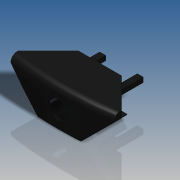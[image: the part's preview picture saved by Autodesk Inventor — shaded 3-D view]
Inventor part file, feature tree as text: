
AUTODESK INVENTOR PART (.ipt)
format: ipt  version: 2016 SP2 (Build 200236200, 236)  size: 336,896 bytes
history: native  units: in
note: dims shown in document units (in); Inventor stores cm internally (conversion verified against a paired STEP export)
features: extrude x6, sketch x5, projected_geometry x3, fillet x2, plane x1
ambient origin geometry x8: Origin, YZ Plane, XZ Plane, XY Plane, X Axis, Y Axis, Z Axis, Center Point
bodies: Solid1 (feature_tree)
feature tree (17):
  extrude  "Extrusion1"  Depth=0.7559in
  extrude  "Extrusion2"  Depth=0.3051in
  extrude  "Extrusion3"  Depth=0.1136in
  plane  "Work Plane1"
  sketch  "Sketch5"  dims[d8=0.014in d9=0.0472in]
  extrude  "Extrusion4"  Depth=0.0472in
  extrude  "Extrusion5"  Depth=0.2205in TaperAngle=0.0deg
  extrude  "Extrusion6"  Depth=0.0378in
  fillet  "Fillet2"  Radius=0.0472in
  fillet  "Fillet1"  Radius=0.0394in
  sketch  "Sketch2"  dims[d0=2.4409in d1=0.7559in]
  sketch  "Sketch3"  dims[d2=0.315in d3=0.3051in]
  sketch  "Sketch4"  dims[d5=0.2693in d6=0.0in d7=0.1136in]
  projected_geometry  "Projected Loop1"
  sketch  "Sketch6"  dims[d10=0.0472in d11=0.2205in d12=0.0in d13=0.0378in d14=0.0472in d15=0.0394in d16=0.378in d17=0.0in d18=0.0507in d19=0.315in d20=0.1276in d21=0.126in d22=0.378in d23=0.0in d24=0.2835in d25=0.0in d26=0.2835in d27=0.0in d28=0.0039in d29=0.0472in d30=0.0547in]
  projected_geometry  "Projected Loop2"
  projected_geometry  "Projected Loop3"
